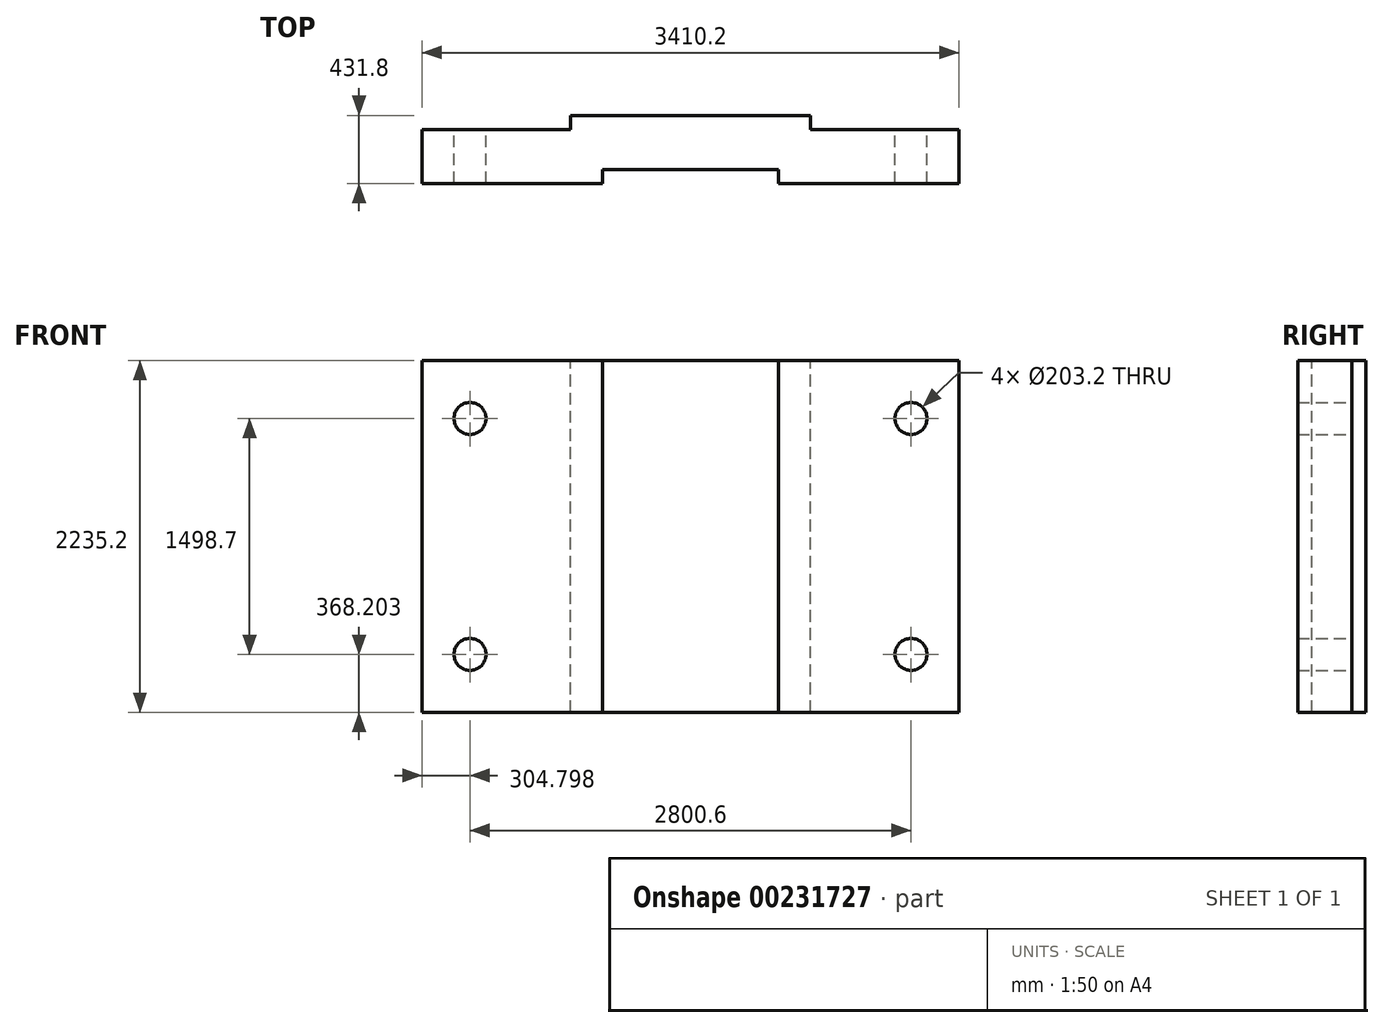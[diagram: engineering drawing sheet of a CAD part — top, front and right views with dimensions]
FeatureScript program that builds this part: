
annotation { "Feature Type Name" : "Feature", "Feature Type Description" : "" }
export const myFeature = defineFeature(function(context is Context, id is Id, definition is map)
    precondition{}
    {
        {
            var Q0;
            Q0=qCreatedBy(makeId("Front.planeOp"),FACE);
            var sketch = newSketch(context, id + "F0", { "sketchPlane" : qUnion([Q0])});
            skLineSegment(sketch, "E0.bottom", {"start": v(558.8, -1117.6) * mm, "end": v(-558.8, -1117.6) * mm});
            skLineSegment(sketch, "E0.top", {"start": v(558.8, 1117.6) * mm, "end": v(-558.8, 1117.6) * mm});
            skLineSegment(sketch, "E0.left", {"start": v(558.8, -1117.6) * mm, "end": v(558.8, 1117.6) * mm});
            skPoint(sketch, "E0.middle", {"position": v(0, 0) * mm});
            skLineSegment(sketch, "E1", {"start": v(558.8, -1117.6) * mm, "end": v(1705.1, -1117.6) * mm});
            skLineSegment(sketch, "E2", {"start": v(558.8, 1117.6) * mm, "end": v(1705.1, 1117.6) * mm});
            skLineSegment(sketch, "E3", {"start": v(1705.1, 1117.6) * mm, "end": v(1705.1, -1117.6) * mm});
            skLineSegment(sketch, "E4", {"start": v(-558.8, 1117.6) * mm, "end": v(-1705.1, 1117.6) * mm});
            skLineSegment(sketch, "E5", {"start": v(-558.8, -1117.6) * mm, "end": v(-1705.1, -1117.6) * mm});
            skCircle(sketch, "E6", {"center": v(-1400.3, 749.3) * mm, "radius": 101.6 * mm});
            skCircle(sketch, "E7", {"center": v(-1400.3, -749.4) * mm, "radius": 101.6 * mm});
            skCircle(sketch, "E8", {"center": v(1400.3, 749.3) * mm, "radius": 101.6 * mm});
            skCircle(sketch, "E9", {"center": v(1400.3, -749.4) * mm, "radius": 101.6 * mm});
            skLineSegment(sketch, "E10", {"start": v(-1705.1, 1117.6) * mm, "end": v(-1705.1, -1117.6) * mm});
            skLineSegment(sketch, "E11", {"start": v(-558.8, 1117.6) * mm, "end": v(-558.8, -1117.6) * mm});
            skSolve(sketch);
        }
        {
            var Q0;
            Q0=makeQuery(id+"F0.imprint","IMPRINT",FACE,{"disambiguationData":[TD([[makeQuery(id+"F0.imprint","IMPRINT",EDGE,{"derivedFrom":sQuery(id+"F0.wireOp",EDGE,"E0.bottom")}),-1.0]])]});
            extrude(context, id + "F1", {"entities" : qUnion([Q0]), "depth" : 331.47 * mm});
        }
        {
            var Q0;
            Q0 = qSketchRegion(id + "F0", true);
            extrude(context, id + "F2", {"entities" : qUnion([Q0]), "operationType" : NewBodyOperationType.ADD, "depth" : 342.9 * mm});
        }
        {
            var Q0;
            {var subQ0=sQuery(id+"F0.wireOp",EDGE,"E0.top");var subQ1=sQuery(id+"F0.wireOp",EDGE,"E0.bottom");Q0=makeQuery(id+"F2.boolean.opBoolean","MERGE",FACE,{"derivedFrom":[makeQuery(id+"F1.opExtrude","CAP_FACE",FACE,{"disambiguationData":[OSD([subQ1,subQ0,sQuery(id+"F0.wireOp",EDGE,"E0.left"),sQuery(id+"F0.wireOp",EDGE,"E11")])],"isStart":true}),makeQuery(id+"F2.opExtrude","CAP_FACE",FACE,{"disambiguationData":[OSD([subQ1,subQ0,sQuery(id+"F0.wireOp",EDGE,"E1"),sQuery(id+"F0.wireOp",EDGE,"E2"),sQuery(id+"F0.wireOp",EDGE,"E3"),sQuery(id+"F0.wireOp",EDGE,"E4"),sQuery(id+"F0.wireOp",EDGE,"E5"),sQuery(id+"F0.wireOp",EDGE,"E6"),sQuery(id+"F0.wireOp",EDGE,"E7"),sQuery(id+"F0.wireOp",EDGE,"E8"),sQuery(id+"F0.wireOp",EDGE,"E9"),sQuery(id+"F0.wireOp",EDGE,"E10")])],"isStart":true})]});}
            var sketch = newSketch(context, id + "F3", { "sketchPlane" : qUnion([Q0])});
            skLineSegment(sketch, "E12.bottom", {"start": v(762.64, -1117.6) * mm, "end": v(-762.64, -1117.6) * mm});
            skLineSegment(sketch, "E12.top", {"start": v(762.64, 1117.6) * mm, "end": v(-762.64, 1117.6) * mm});
            skLineSegment(sketch, "E12.left", {"start": v(762.64, -1117.6) * mm, "end": v(762.64, 1117.6) * mm});
            skLineSegment(sketch, "E12.right", {"start": v(-762.64, -1117.6) * mm, "end": v(-762.64, 1117.6) * mm});
            skPoint(sketch, "E12.middle", {"position": v(0, 0) * mm});
            skSolve(sketch);
        }
        {
            var Q0;
            Q0 = qSketchRegion(id + "F3", true);
            extrude(context, id + "F4", {"entities" : qUnion([Q0]), "operationType" : NewBodyOperationType.ADD, "depth" : 88.9 * mm});
        }
        {
            var Q0;
            Q0=makeQuery(id+"F2.opExtrude","CAP_FACE",FACE,{"disambiguationData":[OSD([sQuery(id+"F0.wireOp",EDGE,"E0.bottom"),sQuery(id+"F0.wireOp",EDGE,"E0.top"),sQuery(id+"F0.wireOp",EDGE,"E1"),sQuery(id+"F0.wireOp",EDGE,"E2"),sQuery(id+"F0.wireOp",EDGE,"E3"),sQuery(id+"F0.wireOp",EDGE,"E4"),sQuery(id+"F0.wireOp",EDGE,"E5"),sQuery(id+"F0.wireOp",EDGE,"E6"),sQuery(id+"F0.wireOp",EDGE,"E7"),sQuery(id+"F0.wireOp",EDGE,"E8"),sQuery(id+"F0.wireOp",EDGE,"E9"),sQuery(id+"F0.wireOp",EDGE,"E10")])],"isStart":false});
            var sketch = newSketch(context, id + "F5", { "sketchPlane" : qUnion([Q0])});
            skLineSegment(sketch, "E13.bottom", {"start": v(558.8, -1117.6) * mm, "end": v(-558.8, -1117.6) * mm});
            skLineSegment(sketch, "E13.top", {"start": v(558.8, 1117.6) * mm, "end": v(-558.8, 1117.6) * mm});
            skLineSegment(sketch, "E13.left", {"start": v(558.8, -1117.6) * mm, "end": v(558.8, 1117.6) * mm});
            skLineSegment(sketch, "E13.right", {"start": v(-558.8, -1117.6) * mm, "end": v(-558.8, 1117.6) * mm});
            skPoint(sketch, "E13.middle", {"position": v(0, 0) * mm});
            skSolve(sketch);
        }
        {
            var Q0;
            Q0=makeQuery(id+"F5.imprint","IMPRINT",FACE,{"disambiguationData":[TD([[makeQuery(id+"F5.imprint","IMPRINT",EDGE,{"derivedFrom":sQuery(id+"F5.wireOp",EDGE,"E13.bottom")}),-1.0]])]});
            extrude(context, id + "F6", {"entities" : qUnion([Q0]), "operationType" : NewBodyOperationType.REMOVE, "oppositeDirection" : true, "depth" : 88.9 * mm});
        }
    });
